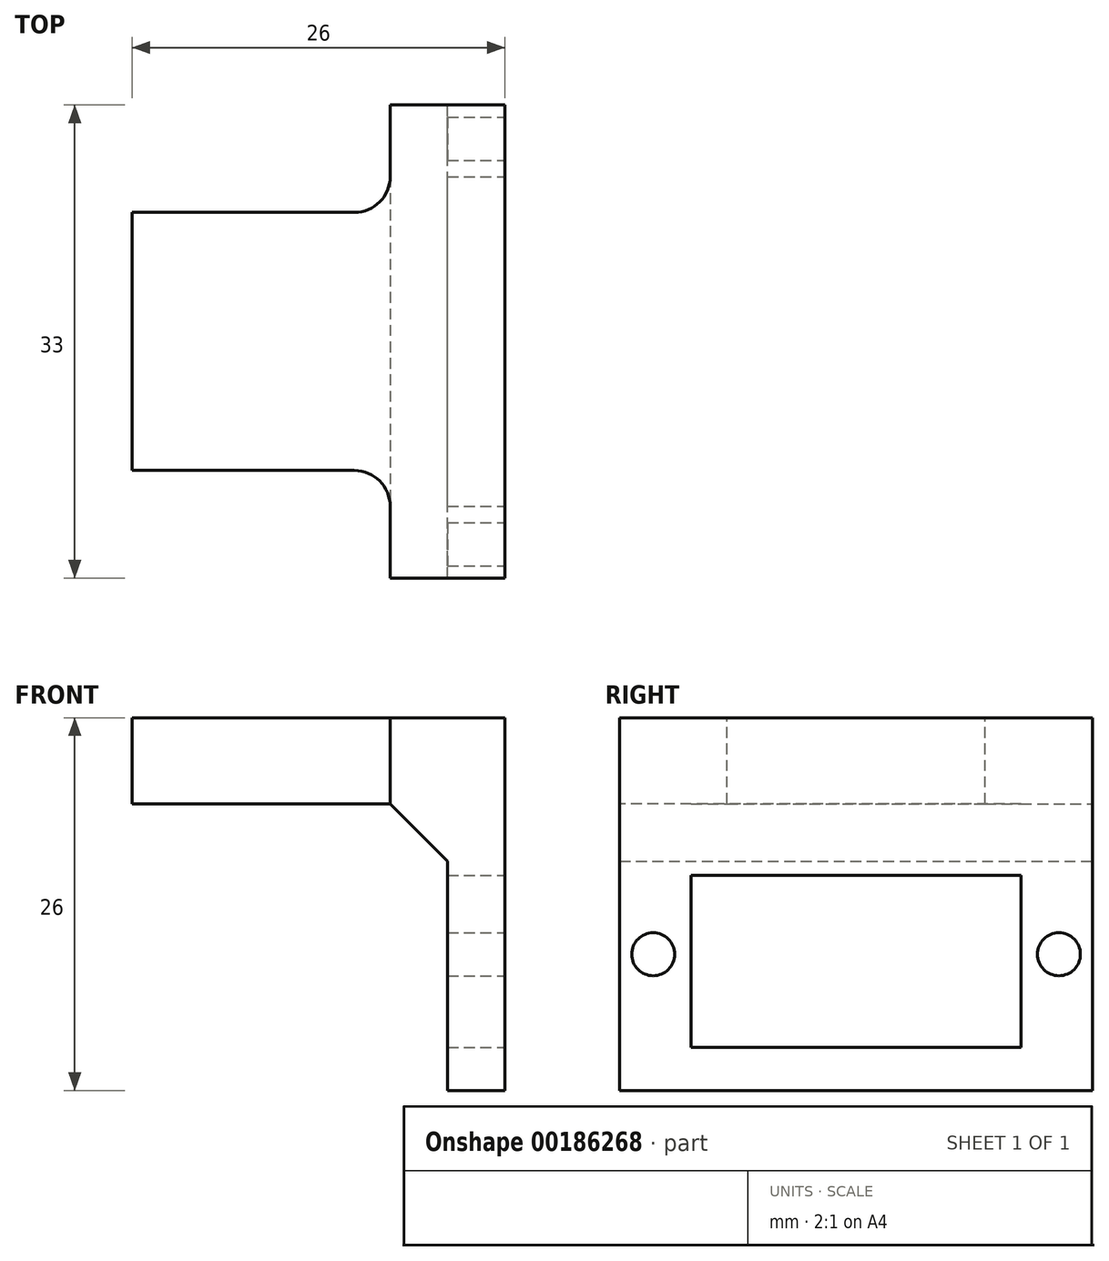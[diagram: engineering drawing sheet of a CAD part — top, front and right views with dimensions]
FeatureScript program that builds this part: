
annotation { "Feature Type Name" : "Feature", "Feature Type Description" : "" }
export const myFeature = defineFeature(function(context is Context, id is Id, definition is map)
    precondition{}
    {
        {
            var Q0;
            Q0=qCreatedBy(makeId("Top.planeOp"),FACE);
            var sketch = newSketch(context, id + "F0", { "sketchPlane" : qUnion([Q0])});
            skLineSegment(sketch, "E0.bottom", {"start": v(0, 0) * mm, "end": v(7, 0) * mm});
            skLineSegment(sketch, "E0.top", {"start": v(0, 18) * mm, "end": v(7, 18) * mm});
            skLineSegment(sketch, "E0.left", {"start": v(0, 0) * mm, "end": v(0, 18) * mm});
            skLineSegment(sketch, "E0.right", {"start": v(7, 0) * mm, "end": v(7, 18) * mm});
            skPoint(sketch, "E1", {"position": v(3, 13) * mm});
            skPoint(sketch, "E2", {"position": v(3, 5) * mm});
            skLineSegment(sketch, "E3.bottom", {"start": v(7, 18) * mm, "end": v(11, 18) * mm});
            skLineSegment(sketch, "E3.top", {"start": v(7, 0) * mm, "end": v(11, 0) * mm});
            skLineSegment(sketch, "E3.left", {"start": v(7, 18) * mm, "end": v(7, 0) * mm});
            skLineSegment(sketch, "E3.right", {"start": v(11, 18) * mm, "end": v(11, 0) * mm});
            skSolve(sketch);
        }
        {
            var Q0;
            Q0=makeQuery(id+"F0.imprint","IMPRINT",FACE,{"disambiguationData":[TD([[makeQuery(id+"F0.imprint","IMPRINT",EDGE,{"derivedFrom":sQuery(id+"F0.wireOp",EDGE,"E3.bottom")}),-1.0]])]});
            extrude(context, id + "F1", {"entities" : qUnion([Q0]), "oppositeDirection" : true, "depth" : 26 * mm});
        }
        {
            var Q0;
            Q0=qSketchRegion(id+"F0",true);
            extrude(context, id + "F2", {"entities" : qUnion([Q0]), "operationType" : NewBodyOperationType.ADD, "oppositeDirection" : true, "depth" : 6 * mm});
        }
        {
            var Q0;
            {var subQ0=sQuery(id+"F0.wireOp",EDGE,"E3.top");Q0=makeQuery(id+"F2.boolean.opBoolean","MERGE",FACE,{"derivedFrom":[makeQuery(id+"F1.opExtrude","SWEPT_FACE",FACE,{"disambiguationData":[OSD([subQ0])]}),makeQuery(id+"F2.opExtrude","SWEPT_FACE",FACE,{"disambiguationData":[OSD([sQuery(id+"F0.wireOp",EDGE,"E0.bottom"),subQ0])]})]});}
            var sketch = newSketch(context, id + "F3", { "sketchPlane" : qUnion([Q0])});
            skPoint(sketch, "E4", {"position": v(11, -8) * mm});
            skPoint(sketch, "E5", {"position": v(7, -8) * mm});
            skLineSegment(sketch, "E6", {"start": v(11, -8) * mm, "end": v(7, -8) * mm});
            skSolve(sketch);
        }
        {
            var Q0;
            {var subQ0=sQuery(id+"F3.wireOp",EDGE,"E6");Q0=makeQuery(id+"F3.imprint","IMPRINT",FACE,{"disambiguationData":[TD([[makeQuery(id+"F3.imprint","IMPRINT",EDGE,{"derivedFrom":subQ0}),1.0]])]});}
            extrude(context, id + "F4", {"entities" : qUnion([Q0]), "operationType" : NewBodyOperationType.ADD, "depth" : 15 * mm});
        }
        {
            var Q0;
            {var subQ0=sQuery(id+"F0.wireOp",EDGE,"E3.bottom");Q0=makeQuery(id+"F2.boolean.opBoolean","MERGE",FACE,{"derivedFrom":[makeQuery(id+"F1.opExtrude","SWEPT_FACE",FACE,{"disambiguationData":[OSD([subQ0])]}),makeQuery(id+"F2.opExtrude","SWEPT_FACE",FACE,{"disambiguationData":[OSD([sQuery(id+"F0.wireOp",EDGE,"E0.top"),subQ0])]})]});}
            var sketch = newSketch(context, id + "F5", { "sketchPlane" : qUnion([Q0])});
            skPoint(sketch, "E7", {"position": v(-7, -8) * mm});
            skPoint(sketch, "E8", {"position": v(-11, -8) * mm});
            skLineSegment(sketch, "E9", {"start": v(-7, -8) * mm, "end": v(-11, -8) * mm});
            skSolve(sketch);
        }
        {
            var Q0;
            {var subQ0=sQuery(id+"F5.wireOp",EDGE,"E9");Q0=makeQuery(id+"F5.imprint","IMPRINT",FACE,{"disambiguationData":[TD([[makeQuery(id+"F5.imprint","IMPRINT",EDGE,{"derivedFrom":subQ0}),1.0]])]});}
            extrude(context, id + "F6", {"entities" : qUnion([Q0]), "operationType" : NewBodyOperationType.ADD, "depth" : 15 * mm});
        }
        {
            var Q0;
            {var subQ0=sQuery(id+"F0.wireOp",EDGE,"E3.right");Q0=makeQuery(id+"F6.boolean.opBoolean","MERGE",FACE,{"derivedFrom":[makeQuery(id+"F4.boolean.opBoolean","MERGE",FACE,{"derivedFrom":[makeQuery(id+"F1.opExtrude","SWEPT_FACE",FACE,{"disambiguationData":[OSD([subQ0])]}),makeQuery(id+"F4.opExtrude","SWEPT_FACE",FACE,{"disambiguationData":[OSD([sQuery(id+"F0.wireOp",EDGE,"E3.top"),subQ0])]})]}),makeQuery(id+"F6.opExtrude","SWEPT_FACE",FACE,{"disambiguationData":[OSD([sQuery(id+"F0.wireOp",EDGE,"E3.bottom"),subQ0])]})]});}
            var sketch = newSketch(context, id + "F7", { "sketchPlane" : qUnion([Q0])});
            skPoint(sketch, "E10", {"position": v(9, 0) * mm});
            skPoint(sketch, "E11", {"position": v(9, -26) * mm});
            skPoint(sketch, "E12", {"position": v(-15, -17) * mm});
            skPoint(sketch, "E13", {"position": v(33, -17) * mm});
            skPoint(sketch, "E14", {"position": v(-15, -23) * mm});
            skPoint(sketch, "E15", {"position": v(33, -23) * mm});
            skPoint(sketch, "E16", {"position": v(-15, -11) * mm});
            skPoint(sketch, "E17", {"position": v(33, -11) * mm});
            skLineSegment(sketch, "E18", {"start": v(-15, -11) * mm, "end": v(33, -11) * mm});
            skLineSegment(sketch, "E19", {"start": v(-15, -23) * mm, "end": v(33, -23) * mm});
            skLineSegment(sketch, "E20", {"start": v(9, 0) * mm, "end": v(9, -26) * mm});
            skPoint(sketch, "E21", {"position": v(9, -11) * mm});
            skPoint(sketch, "E22", {"position": v(20.5, -11) * mm});
            skPoint(sketch, "E23", {"position": v(-2.5, -11) * mm});
            skLineSegment(sketch, "E24", {"start": v(-2.5, -11) * mm, "end": v(-2.5, -23) * mm});
            skLineSegment(sketch, "E25", {"start": v(20.5, -11) * mm, "end": v(20.5, -23) * mm});
            skLineSegment(sketch, "E26", {"start": v(-15, -17) * mm, "end": v(33, -17) * mm});
            skPoint(sketch, "E27", {"position": v(-15, -16.5) * mm});
            skPoint(sketch, "E28", {"position": v(33, -16.5) * mm});
            skLineSegment(sketch, "E29", {"start": v(-15, -16.5) * mm, "end": v(33, -16.5) * mm});
            skPoint(sketch, "E30", {"position": v(-5.15, -16.5) * mm});
            skPoint(sketch, "E31", {"position": v(-2.5, -17) * mm});
            skPoint(sketch, "E32", {"position": v(20.5, -17) * mm});
            skPoint(sketch, "E33", {"position": v(23.15, -16.5) * mm});
            skCircle(sketch, "E34", {"center": v(23.15, -16.5) * mm, "radius": 1.5 * mm});
            skCircle(sketch, "E35", {"center": v(-5.15, -16.5) * mm, "radius": 1.5 * mm});
            skSolve(sketch);
        }
        {
            var Q0;
            {var subQ0=sQuery(id+"F7.wireOp",EDGE,"E24");var subQ1=sQuery(id+"F7.wireOp",EDGE,"E18");var subQ2=makeQuery(id+"F7.imprint","INTERSECT",VERTEX,{"derivedFrom":[subQ1,subQ0]});Q0=makeQuery(id+"F7.imprint","IMPRINT",FACE,{"disambiguationData":[TD([[makeQuery(id+"F7.imprint","IMPRINT",EDGE,{"disambiguationData":[TD([[subQ2,-1.0]])],"derivedFrom":subQ1}),-1.0]])]});}
            var Q1;
            {var subQ0=sQuery(id+"F7.wireOp",EDGE,"E25");var subQ1=sQuery(id+"F7.wireOp",EDGE,"E18");var subQ2=makeQuery(id+"F7.imprint","INTERSECT",VERTEX,{"derivedFrom":[subQ1,subQ0]});Q1=makeQuery(id+"F7.imprint","IMPRINT",FACE,{"disambiguationData":[TD([[makeQuery(id+"F7.imprint","IMPRINT",EDGE,{"disambiguationData":[TD([[subQ2,1.0]])],"derivedFrom":subQ1}),-1.0]])]});}
            var Q2;
            {var subQ0=sQuery(id+"F7.wireOp",EDGE,"E34");var subQ1=sQuery(id+"F7.wireOp",EDGE,"E26");var subQ2=makeQuery(id+"F7.imprint","INTERSECT",VERTEX,{"disambiguationData":[OD(0.0)],"derivedFrom":[subQ1,subQ0]});Q2=makeQuery(id+"F7.imprint","IMPRINT",FACE,{"disambiguationData":[TD([[makeQuery(id+"F7.imprint","IMPRINT",EDGE,{"disambiguationData":[TD([[subQ2,-1.0]])],"derivedFrom":subQ1}),-1.0]])]});}
            var Q3;
            {var subQ0=sQuery(id+"F7.wireOp",EDGE,"E34");var subQ1=sQuery(id+"F7.wireOp",EDGE,"E26");var subQ2=makeQuery(id+"F7.imprint","INTERSECT",VERTEX,{"disambiguationData":[OD(0.0)],"derivedFrom":[subQ1,subQ0]});Q3=makeQuery(id+"F7.imprint","IMPRINT",FACE,{"disambiguationData":[TD([[makeQuery(id+"F7.imprint","IMPRINT",EDGE,{"disambiguationData":[TD([[subQ2,-1.0]])],"derivedFrom":subQ1}),1.0]])]});}
            var Q4;
            {var subQ0=sQuery(id+"F7.wireOp",EDGE,"E34");var subQ1=sQuery(id+"F7.wireOp",EDGE,"E29");var subQ2=makeQuery(id+"F7.imprint","INTERSECT",VERTEX,{"disambiguationData":[OD(0.0)],"derivedFrom":[subQ1,subQ0]});Q4=makeQuery(id+"F7.imprint","IMPRINT",FACE,{"disambiguationData":[TD([[makeQuery(id+"F7.imprint","IMPRINT",EDGE,{"disambiguationData":[TD([[subQ2,-1.0]])],"derivedFrom":subQ1}),1.0]])]});}
            var Q5;
            {var subQ0=sQuery(id+"F7.wireOp",EDGE,"E25");var subQ1=sQuery(id+"F7.wireOp",EDGE,"E19");var subQ2=makeQuery(id+"F7.imprint","INTERSECT",VERTEX,{"derivedFrom":[subQ1,subQ0]});Q5=makeQuery(id+"F7.imprint","IMPRINT",FACE,{"disambiguationData":[TD([[makeQuery(id+"F7.imprint","IMPRINT",EDGE,{"disambiguationData":[TD([[subQ2,1.0]])],"derivedFrom":subQ1}),1.0]])]});}
            var Q6;
            {var subQ0=sQuery(id+"F7.wireOp",EDGE,"E29");var subQ1=sQuery(id+"F7.wireOp",EDGE,"E20");var subQ2=makeQuery(id+"F7.imprint","INTERSECT",VERTEX,{"derivedFrom":[subQ1,subQ0]});Q6=makeQuery(id+"F7.imprint","IMPRINT",FACE,{"disambiguationData":[TD([[makeQuery(id+"F7.imprint","IMPRINT",EDGE,{"disambiguationData":[TD([[subQ2,-1.0]])],"derivedFrom":subQ1}),1.0]])]});}
            var Q7;
            {var subQ0=sQuery(id+"F7.wireOp",EDGE,"E24");var subQ1=sQuery(id+"F7.wireOp",EDGE,"E19");var subQ2=makeQuery(id+"F7.imprint","INTERSECT",VERTEX,{"derivedFrom":[subQ1,subQ0]});Q7=makeQuery(id+"F7.imprint","IMPRINT",FACE,{"disambiguationData":[TD([[makeQuery(id+"F7.imprint","IMPRINT",EDGE,{"disambiguationData":[TD([[subQ2,-1.0]])],"derivedFrom":subQ1}),1.0]])]});}
            var Q8;
            {var subQ0=sQuery(id+"F7.wireOp",EDGE,"E29");var subQ1=sQuery(id+"F7.wireOp",EDGE,"E20");var subQ2=makeQuery(id+"F7.imprint","INTERSECT",VERTEX,{"derivedFrom":[subQ1,subQ0]});Q8=makeQuery(id+"F7.imprint","IMPRINT",FACE,{"disambiguationData":[TD([[makeQuery(id+"F7.imprint","IMPRINT",EDGE,{"disambiguationData":[TD([[subQ2,-1.0]])],"derivedFrom":subQ1}),-1.0]])]});}
            var Q9;
            {var subQ0=sQuery(id+"F7.wireOp",EDGE,"E35");var subQ1=sQuery(id+"F7.wireOp",EDGE,"E29");var subQ2=makeQuery(id+"F7.imprint","INTERSECT",VERTEX,{"disambiguationData":[OD(0.0)],"derivedFrom":[subQ1,subQ0]});Q9=makeQuery(id+"F7.imprint","IMPRINT",FACE,{"disambiguationData":[TD([[makeQuery(id+"F7.imprint","IMPRINT",EDGE,{"disambiguationData":[TD([[subQ2,-1.0]])],"derivedFrom":subQ1}),1.0]])]});}
            var Q10;
            {var subQ0=sQuery(id+"F7.wireOp",EDGE,"E35");var subQ1=sQuery(id+"F7.wireOp",EDGE,"E26");var subQ2=makeQuery(id+"F7.imprint","INTERSECT",VERTEX,{"disambiguationData":[OD(0.0)],"derivedFrom":[subQ1,subQ0]});Q10=makeQuery(id+"F7.imprint","IMPRINT",FACE,{"disambiguationData":[TD([[makeQuery(id+"F7.imprint","IMPRINT",EDGE,{"disambiguationData":[TD([[subQ2,-1.0]])],"derivedFrom":subQ1}),1.0]])]});}
            var Q11;
            {var subQ0=sQuery(id+"F7.wireOp",EDGE,"E35");var subQ1=sQuery(id+"F7.wireOp",EDGE,"E26");var subQ2=makeQuery(id+"F7.imprint","INTERSECT",VERTEX,{"disambiguationData":[OD(0.0)],"derivedFrom":[subQ1,subQ0]});Q11=makeQuery(id+"F7.imprint","IMPRINT",FACE,{"disambiguationData":[TD([[makeQuery(id+"F7.imprint","IMPRINT",EDGE,{"disambiguationData":[TD([[subQ2,-1.0]])],"derivedFrom":subQ1}),-1.0]])]});}
            extrude(context, id + "F8", {"entities" : qUnion([Q0, Q1, Q2, Q3, Q4, Q5, Q6, Q7, Q8, Q9, Q10, Q11]), "operationType" : NewBodyOperationType.REMOVE, "oppositeDirection" : true, "depth" : 25 * mm});
        }
        {
            var Q0;
            Q0=makeQuery(id+"F2.opExtrude","SWEPT_FACE",FACE,{"disambiguationData":[OSD([sQuery(id+"F0.wireOp",EDGE,"E0.left")])]});
            extrude(context, id + "F9", {"entities" : qUnion([Q0]), "operationType" : NewBodyOperationType.ADD, "depth" : 15 * mm});
        }
        {
            var Q0;
            {var subQ0=sQuery(id+"F0.wireOp",EDGE,"E0.bottom");var subQ1=sQuery(id+"F0.wireOp",EDGE,"E3.top");Q0=makeQuery(id+"F9.boolean.opBoolean","MERGE",FACE,{"derivedFrom":[makeQuery(id+"F2.boolean.opBoolean","MERGE",FACE,{"derivedFrom":[makeQuery(id+"F1.opExtrude","SWEPT_FACE",FACE,{"disambiguationData":[OSD([subQ1])]}),makeQuery(id+"F2.opExtrude","SWEPT_FACE",FACE,{"disambiguationData":[OSD([subQ0,subQ1])]})]}),makeQuery(id+"F9.opExtrude","SWEPT_FACE",FACE,{"disambiguationData":[OSD([subQ0,sQuery(id+"F0.wireOp",EDGE,"E0.left")])]})]});}
            extrude(context, id + "F10", {"entities" : qUnion([Q0]), "operationType" : NewBodyOperationType.ADD, "depth" : 18 * mm});
        }
        {
            var Q0;
            {var subQ0=sQuery(id+"F0.wireOp",EDGE,"E0.top");var subQ1=sQuery(id+"F0.wireOp",EDGE,"E3.bottom");Q0=makeQuery(id+"F9.boolean.opBoolean","MERGE",FACE,{"derivedFrom":[makeQuery(id+"F2.boolean.opBoolean","MERGE",FACE,{"derivedFrom":[makeQuery(id+"F1.opExtrude","SWEPT_FACE",FACE,{"disambiguationData":[OSD([subQ1])]}),makeQuery(id+"F2.opExtrude","SWEPT_FACE",FACE,{"disambiguationData":[OSD([subQ0,subQ1])]})]}),makeQuery(id+"F9.opExtrude","SWEPT_FACE",FACE,{"disambiguationData":[OSD([subQ0,sQuery(id+"F0.wireOp",EDGE,"E0.left")])]})]});}
            extrude(context, id + "F11", {"entities" : qUnion([Q0]), "operationType" : NewBodyOperationType.REMOVE, "oppositeDirection" : true, "depth" : 2 * mm});
        }
        {
            var Q0;
            Q0=makeQuery(id+"F4.opExtrude","CAP_FACE",FACE,{"disambiguationData":[OSD([sQuery(id+"F0.wireOp",EDGE,"E0.bottom"),sQuery(id+"F0.wireOp",EDGE,"E3.top"),sQuery(id+"F0.wireOp",EDGE,"E3.left"),sQuery(id+"F0.wireOp",EDGE,"E3.right"),sQuery(id+"F3.wireOp",EDGE,"E6")])],"isStart":false});
            extrude(context, id + "F12", {"entities" : qUnion([Q0]), "operationType" : NewBodyOperationType.REMOVE, "oppositeDirection" : true, "depth" : 6 * mm});
        }
        {
            var Q0;
            Q0=makeQuery(id+"F6.opExtrude","CAP_FACE",FACE,{"disambiguationData":[OSD([sQuery(id+"F0.wireOp",EDGE,"E0.top"),sQuery(id+"F0.wireOp",EDGE,"E3.bottom"),sQuery(id+"F0.wireOp",EDGE,"E3.left"),sQuery(id+"F0.wireOp",EDGE,"E3.right"),sQuery(id+"F5.wireOp",EDGE,"E9")])],"isStart":false});
            extrude(context, id + "F13", {"entities" : qUnion([Q0]), "operationType" : NewBodyOperationType.REMOVE, "oppositeDirection" : true, "depth" : 6 * mm});
        }
        {
            var Q0;
            Q0=makeQuery(id+"F11.boolean.opBoolean","COPY",FACE,{"derivedFrom":makeQuery(id+"F11.opExtrude","CAP_FACE",FACE,{"disambiguationData":[OSD([sQuery(id+"F0.wireOp",EDGE,"E0.top"),sQuery(id+"F0.wireOp",EDGE,"E0.left"),sQuery(id+"F0.wireOp",EDGE,"E3.bottom")])],"isStart":false})});
            extrude(context, id + "F14", {"entities" : qUnion([Q0]), "operationType" : NewBodyOperationType.ADD, "depth" : 11 * mm});
        }
        {
            var Q0;
            {var subQ0=sQuery(id+"F0.wireOp",EDGE,"E3.right");var subQ1=sQuery(id+"F0.wireOp",EDGE,"E3.bottom");var subQ2=sQuery(id+"F0.wireOp",EDGE,"E3.top");Q0=makeQuery(id+"F14.boolean.opBoolean","MERGE",FACE,{"derivedFrom":[makeQuery(id+"F10.boolean.opBoolean","MERGE",FACE,{"derivedFrom":[makeQuery(id+"F6.boolean.opBoolean","MERGE",FACE,{"derivedFrom":[makeQuery(id+"F4.boolean.opBoolean","MERGE",FACE,{"derivedFrom":[makeQuery(id+"F1.opExtrude","SWEPT_FACE",FACE,{"disambiguationData":[OSD([subQ0])]}),makeQuery(id+"F4.opExtrude","SWEPT_FACE",FACE,{"disambiguationData":[OSD([subQ2,subQ0])]})]}),makeQuery(id+"F6.opExtrude","SWEPT_FACE",FACE,{"disambiguationData":[OSD([subQ1,subQ0])]})]}),makeQuery(id+"F10.opExtrude","SWEPT_FACE",FACE,{"disambiguationData":[OSD([subQ2,subQ0])]})]}),makeQuery(id+"F14.opExtrude","SWEPT_FACE",FACE,{"disambiguationData":[OSD([subQ1,subQ0])]})]});}
            var sketch = newSketch(context, id + "F15", { "sketchPlane" : qUnion([Q0])});
            skPoint(sketch, "E36", {"position": v(-9, -8) * mm});
            skLineSegment(sketch, "E37", {"start": v(-9, -8) * mm, "end": v(-9, 0) * mm});
            skSolve(sketch);
        }
        {
            var Q0;
            {var subQ0=sQuery(id+"F15.wireOp",EDGE,"E37");Q0=makeQuery(id+"F15.imprint","IMPRINT",FACE,{"disambiguationData":[TD([[makeQuery(id+"F15.imprint","IMPRINT",EDGE,{"derivedFrom":subQ0}),1.0]])]});}
            extrude(context, id + "F16", {"entities" : qUnion([Q0]), "operationType" : NewBodyOperationType.REMOVE, "oppositeDirection" : true, "depth" : 30 * mm});
        }
        {
            var Q0;
            {var subQ0=sQuery(id+"F0.wireOp",EDGE,"E0.left");var subQ1=sQuery(id+"F0.wireOp",EDGE,"E0.top");var subQ2=sQuery(id+"F0.wireOp",EDGE,"E3.bottom");var subQ3=sQuery(id+"F0.wireOp",EDGE,"E0.bottom");var subQ4=sQuery(id+"F0.wireOp",EDGE,"E3.top");var subQ5=sQuery(id+"F0.wireOp",EDGE,"E3.right");Q0=makeQuery(id+"F14.boolean.opBoolean","MERGE",FACE,{"derivedFrom":[makeQuery(id+"F10.boolean.opBoolean","MERGE",FACE,{"derivedFrom":[makeQuery(id+"F9.boolean.opBoolean","MERGE",FACE,{"derivedFrom":[makeQuery(id+"F2.boolean.opBoolean","MERGE",FACE,{"derivedFrom":[makeQuery(id+"F1.opExtrude","CAP_FACE",FACE,{"disambiguationData":[OSD([subQ2,subQ4,sQuery(id+"F0.wireOp",EDGE,"E3.left"),subQ5])],"isStart":true}),makeQuery(id+"F2.opExtrude","CAP_FACE",FACE,{"disambiguationData":[OSD([subQ3,subQ1,subQ0,subQ2,subQ4,subQ5])],"isStart":true})]}),makeQuery(id+"F9.opExtrude","SWEPT_FACE",FACE,{"disambiguationData":[OSD([subQ0]),TDD([makeQuery(id+"F2.opExtrude","CAP_EDGE",EDGE,{"disambiguationData":[OSD([subQ0])],"isStart":true})])]})]}),makeQuery(id+"F10.opExtrude","SWEPT_FACE",FACE,{"disambiguationData":[OSD([subQ3,subQ0,subQ4]),TDD([makeQuery(id+"F9.boolean.opBoolean","MERGE",EDGE,{"derivedFrom":[makeQuery(id+"F2.boolean.opBoolean","MERGE",EDGE,{"derivedFrom":[makeQuery(id+"F1.opExtrude","CAP_EDGE",EDGE,{"disambiguationData":[OSD([subQ4])],"isStart":true}),makeQuery(id+"F2.opExtrude","CAP_EDGE",EDGE,{"disambiguationData":[OSD([subQ3,subQ4])],"isStart":true})]}),makeQuery(id+"F9.opExtrude","SWEPT_EDGE",EDGE,{"disambiguationData":[OSD([subQ3,subQ0]),TDD([makeQuery(id+"F2.opExtrude","CAP_VERTEX",VERTEX,{"disambiguationData":[OSD([subQ3,subQ0])],"isStart":true})])]})]})])]})]}),makeQuery(id+"F14.opExtrude","SWEPT_FACE",FACE,{"disambiguationData":[OSD([subQ1,subQ0,subQ2]),TDD([makeQuery(id+"F11.boolean.opBoolean","COPY",EDGE,{"derivedFrom":makeQuery(id+"F11.opExtrude","CAP_EDGE",EDGE,{"disambiguationData":[OSD([subQ1,subQ0,subQ2]),TDD([makeQuery(id+"F9.boolean.opBoolean","MERGE",EDGE,{"derivedFrom":[makeQuery(id+"F2.boolean.opBoolean","MERGE",EDGE,{"derivedFrom":[makeQuery(id+"F1.opExtrude","CAP_EDGE",EDGE,{"disambiguationData":[OSD([subQ2])],"isStart":true}),makeQuery(id+"F2.opExtrude","CAP_EDGE",EDGE,{"disambiguationData":[OSD([subQ1,subQ2])],"isStart":true})]}),makeQuery(id+"F9.opExtrude","SWEPT_EDGE",EDGE,{"disambiguationData":[OSD([subQ1,subQ0]),TDD([makeQuery(id+"F2.opExtrude","CAP_VERTEX",VERTEX,{"disambiguationData":[OSD([subQ1,subQ0])],"isStart":true})])]})]})])],"isStart":false})})])]})]});}
            var sketch = newSketch(context, id + "F17", { "sketchPlane" : qUnion([Q0])});
            skPoint(sketch, "E38", {"position": v(-15, 9) * mm});
            skPoint(sketch, "E39", {"position": v(-15, 18) * mm});
            skPoint(sketch, "E40", {"position": v(-15, 0) * mm});
            skPoint(sketch, "E41", {"position": v(-11, 0) * mm});
            skLineSegment(sketch, "E42", {"start": v(-11, 0) * mm, "end": v(-11, 20.04) * mm});
            skPoint(sketch, "E43", {"position": v(-11, 5) * mm});
            skPoint(sketch, "E44", {"position": v(-11, 13) * mm});
            skPoint(sketch, "E45", {"position": v(-11, 17.97) * mm});
            skSolve(sketch);
        }
        {
            var Q0;
            Q0=sQuery(id+"F17.wireOp",VERTEX,"E44");
            var Q1;
            Q1=sQuery(id+"F17.wireOp",VERTEX,"E43");
            var Q2;
            Q2=makeQuery(id+"F1.opExtrude","SWEPT_BODY",BODY,{"disambiguationData":[OSD([sQuery(id+"F0.wireOp",EDGE,"E3.bottom"),sQuery(id+"F0.wireOp",EDGE,"E3.top"),sQuery(id+"F0.wireOp",EDGE,"E3.left"),sQuery(id+"F0.wireOp",EDGE,"E3.right")])]});
            hole(context, id + "F18", {"style" : HoleStyle.SIMPLE, "endStyle" : HoleEndStyle.THROUGH, "holeDiameter" : 3.5 * mm, "tappedDepth" : 12 * mm, "tapClearance" : 3, "startFromSketch" : true, "locations" : qUnion([Q0, Q1]), "scope" : qUnion([Q2])});
        }
        {
            var Q0;
            Q0=makeQuery(id+"F16.boolean.opBoolean","MERGE",FACE,{"derivedFrom":[makeQuery(id+"F12.boolean.opBoolean","COPY",FACE,{"derivedFrom":makeQuery(id+"F12.opExtrude","CAP_FACE",FACE,{"disambiguationData":[OSD([sQuery(id+"F0.wireOp",EDGE,"E0.bottom"),sQuery(id+"F0.wireOp",EDGE,"E3.top"),sQuery(id+"F0.wireOp",EDGE,"E3.left"),sQuery(id+"F0.wireOp",EDGE,"E3.right"),sQuery(id+"F3.wireOp",EDGE,"E6")])],"isStart":false})}),makeQuery(id+"F16.opExtrude","SWEPT_FACE",FACE,{"disambiguationData":[OSD([sQuery(id+"F15.wireOp",EDGE,"E37")])]})]});
            var sketch = newSketch(context, id + "F19", { "sketchPlane" : qUnion([Q0])});
            skPoint(sketch, "E46", {"position": v(3, -6) * mm});
            skLineSegment(sketch, "E47", {"start": v(3, -6) * mm, "end": v(3, 0) * mm});
            skSolve(sketch);
        }
        {
            var Q0;
            {var subQ0=sQuery(id+"F19.wireOp",EDGE,"E47");Q0=makeQuery(id+"F19.imprint","IMPRINT",FACE,{"disambiguationData":[TD([[makeQuery(id+"F19.imprint","IMPRINT",EDGE,{"derivedFrom":subQ0}),1.0]])]});}
            extrude(context, id + "F20", {"entities" : qUnion([Q0]), "operationType" : NewBodyOperationType.REMOVE, "oppositeDirection" : true, "depth" : 9 * mm});
        }
        {
            var Q0;
            {var subQ0=sQuery(id+"F0.wireOp",EDGE,"E3.bottom");var subQ1=sQuery(id+"F0.wireOp",EDGE,"E0.top");Q0=makeQuery(id+"F14.boolean.opBoolean","MERGE",FACE,{"derivedFrom":[makeQuery(id+"F13.boolean.opBoolean","COPY",FACE,{"derivedFrom":makeQuery(id+"F13.opExtrude","CAP_FACE",FACE,{"disambiguationData":[OSD([subQ1,subQ0,sQuery(id+"F0.wireOp",EDGE,"E3.left"),sQuery(id+"F0.wireOp",EDGE,"E3.right"),sQuery(id+"F5.wireOp",EDGE,"E9")])],"isStart":false})}),makeQuery(id+"F14.opExtrude","CAP_FACE",FACE,{"disambiguationData":[OSD([subQ1,sQuery(id+"F0.wireOp",EDGE,"E0.left"),subQ0])],"isStart":false})]});}
            var sketch = newSketch(context, id + "F21", { "sketchPlane" : qUnion([Q0])});
            skPoint(sketch, "E48", {"position": v(-3, -6) * mm});
            skLineSegment(sketch, "E49", {"start": v(-3, -6) * mm, "end": v(-3, 0) * mm});
            skSolve(sketch);
        }
        {
            var Q0;
            {var subQ0=sQuery(id+"F21.wireOp",EDGE,"E49");Q0=makeQuery(id+"F21.imprint","IMPRINT",FACE,{"disambiguationData":[TD([[makeQuery(id+"F21.imprint","IMPRINT",EDGE,{"derivedFrom":subQ0}),-1.0]])]});}
            extrude(context, id + "F22", {"entities" : qUnion([Q0]), "operationType" : NewBodyOperationType.REMOVE, "oppositeDirection" : true, "depth" : 9 * mm});
        }
        {
            var Q0;
            {var subQ0=sQuery(id+"F0.wireOp",EDGE,"E3.right");var subQ1=sQuery(id+"F0.wireOp",EDGE,"E3.left");var subQ2=sQuery(id+"F0.wireOp",EDGE,"E3.top");var subQ3=sQuery(id+"F0.wireOp",EDGE,"E3.bottom");var subQ4=sQuery(id+"F0.wireOp",EDGE,"E0.left");var subQ5=sQuery(id+"F0.wireOp",EDGE,"E0.top");var subQ6=sQuery(id+"F0.wireOp",EDGE,"E0.bottom");Q0=makeQuery(id+"F14.boolean.opBoolean","MERGE",EDGE,{"derivedFrom":[makeQuery(id+"F10.boolean.opBoolean","MERGE",EDGE,{"derivedFrom":[makeQuery(id+"F2.boolean.opBoolean","INTERSECT",EDGE,{"derivedFrom":[makeQuery(id+"F1.opExtrude","SWEPT_FACE",FACE,{"disambiguationData":[OSD([subQ1])]}),makeQuery(id+"F2.opExtrude","CAP_FACE",FACE,{"disambiguationData":[OSD([subQ6,subQ5,subQ4,subQ3,subQ2,subQ0])],"isStart":false})]}),makeQuery(id+"F10.opExtrude","SWEPT_EDGE",EDGE,{"disambiguationData":[OSD([subQ6,subQ5,subQ4,subQ3,subQ2,subQ1,subQ0])]})]}),makeQuery(id+"F14.opExtrude","SWEPT_EDGE",EDGE,{"disambiguationData":[OSD([subQ6,subQ5,subQ4,subQ3,subQ2,subQ1,subQ0])]})]});}
            chamfer(context, id + "F23", {"entities" : qUnion([Q0]), "width" : 4 * mm, "tangentPropagation" : true});
        }
        {
            var Q0;
            Q0=makeQuery(id+"F16.boolean.opBoolean","MERGE",FACE,{"derivedFrom":[makeQuery(id+"F12.boolean.opBoolean","COPY",FACE,{"derivedFrom":makeQuery(id+"F12.opExtrude","CAP_FACE",FACE,{"disambiguationData":[OSD([sQuery(id+"F0.wireOp",EDGE,"E0.bottom"),sQuery(id+"F0.wireOp",EDGE,"E3.top"),sQuery(id+"F0.wireOp",EDGE,"E3.left"),sQuery(id+"F0.wireOp",EDGE,"E3.right"),sQuery(id+"F3.wireOp",EDGE,"E6")])],"isStart":false})}),makeQuery(id+"F16.opExtrude","SWEPT_FACE",FACE,{"disambiguationData":[OSD([sQuery(id+"F15.wireOp",EDGE,"E37")])]})]});
            extrude(context, id + "F24", {"entities" : qUnion([Q0]), "operationType" : NewBodyOperationType.REMOVE, "oppositeDirection" : true, "depth" : 1.5 * mm});
        }
        {
            var Q0;
            {var subQ0=sQuery(id+"F0.wireOp",EDGE,"E3.bottom");var subQ1=sQuery(id+"F0.wireOp",EDGE,"E0.top");Q0=makeQuery(id+"F14.boolean.opBoolean","MERGE",FACE,{"derivedFrom":[makeQuery(id+"F13.boolean.opBoolean","COPY",FACE,{"derivedFrom":makeQuery(id+"F13.opExtrude","CAP_FACE",FACE,{"disambiguationData":[OSD([subQ1,subQ0,sQuery(id+"F0.wireOp",EDGE,"E3.left"),sQuery(id+"F0.wireOp",EDGE,"E3.right"),sQuery(id+"F5.wireOp",EDGE,"E9")])],"isStart":false})}),makeQuery(id+"F14.opExtrude","CAP_FACE",FACE,{"disambiguationData":[OSD([subQ1,sQuery(id+"F0.wireOp",EDGE,"E0.left"),subQ0])],"isStart":false})]});}
            extrude(context, id + "F25", {"entities" : qUnion([Q0]), "operationType" : NewBodyOperationType.REMOVE, "oppositeDirection" : true, "depth" : 1.5 * mm});
        }
        {
            var Q0;
            Q0=makeQuery(id+"F25.boolean.opBoolean","COPY",EDGE,{"derivedFrom":makeQuery(id+"F25.opExtrude","CAP_EDGE",EDGE,{"disambiguationData":[OSD([sQuery(id+"F0.wireOp",EDGE,"E3.bottom")])],"isStart":false})});
            var Q1;
            Q1=makeQuery(id+"F25.boolean.opBoolean","COPY",EDGE,{"derivedFrom":makeQuery(id+"F25.opExtrude","CAP_EDGE",EDGE,{"disambiguationData":[OSD([sQuery(id+"F21.wireOp",EDGE,"E49")])],"isStart":false})});
            var Q2;
            Q2=makeQuery(id+"F22.boolean.opBoolean","COPY",EDGE,{"derivedFrom":makeQuery(id+"F22.opExtrude","CAP_EDGE",EDGE,{"disambiguationData":[OSD([sQuery(id+"F0.wireOp",EDGE,"E0.top"),sQuery(id+"F0.wireOp",EDGE,"E0.left")])],"isStart":false})});
            var Q3;
            Q3=makeQuery(id+"F20.boolean.opBoolean","COPY",EDGE,{"derivedFrom":makeQuery(id+"F20.opExtrude","CAP_EDGE",EDGE,{"disambiguationData":[OSD([sQuery(id+"F0.wireOp",EDGE,"E0.bottom"),sQuery(id+"F0.wireOp",EDGE,"E0.top"),sQuery(id+"F0.wireOp",EDGE,"E0.left"),sQuery(id+"F15.wireOp",EDGE,"E37")])],"isStart":false})});
            var Q4;
            Q4=makeQuery(id+"F24.boolean.opBoolean","COPY",EDGE,{"derivedFrom":makeQuery(id+"F24.opExtrude","CAP_EDGE",EDGE,{"disambiguationData":[OSD([sQuery(id+"F0.wireOp",EDGE,"E3.top")])],"isStart":false})});
            var Q5;
            Q5=makeQuery(id+"F24.boolean.opBoolean","COPY",EDGE,{"derivedFrom":makeQuery(id+"F24.opExtrude","CAP_EDGE",EDGE,{"disambiguationData":[OSD([sQuery(id+"F19.wireOp",EDGE,"E47")])],"isStart":false})});
            var Q6;
            Q6=makeQuery(id+"F20.boolean.opBoolean","COPY",EDGE,{"derivedFrom":makeQuery(id+"F20.opExtrude","CAP_EDGE",EDGE,{"disambiguationData":[OSD([sQuery(id+"F19.wireOp",EDGE,"E47")])],"isStart":false})});
            var Q7;
            Q7=makeQuery(id+"F22.boolean.opBoolean","COPY",EDGE,{"derivedFrom":makeQuery(id+"F22.opExtrude","CAP_EDGE",EDGE,{"disambiguationData":[OSD([sQuery(id+"F21.wireOp",EDGE,"E49")])],"isStart":false})});
            fillet(context, id + "F26", {"entities" : qUnion([Q0, Q1, Q2, Q3, Q4, Q5, Q6, Q7]), "radius" : 2.5 * mm, "tangentPropagation" : true, "allowEdgeOverflow" : false});
        }
    });
